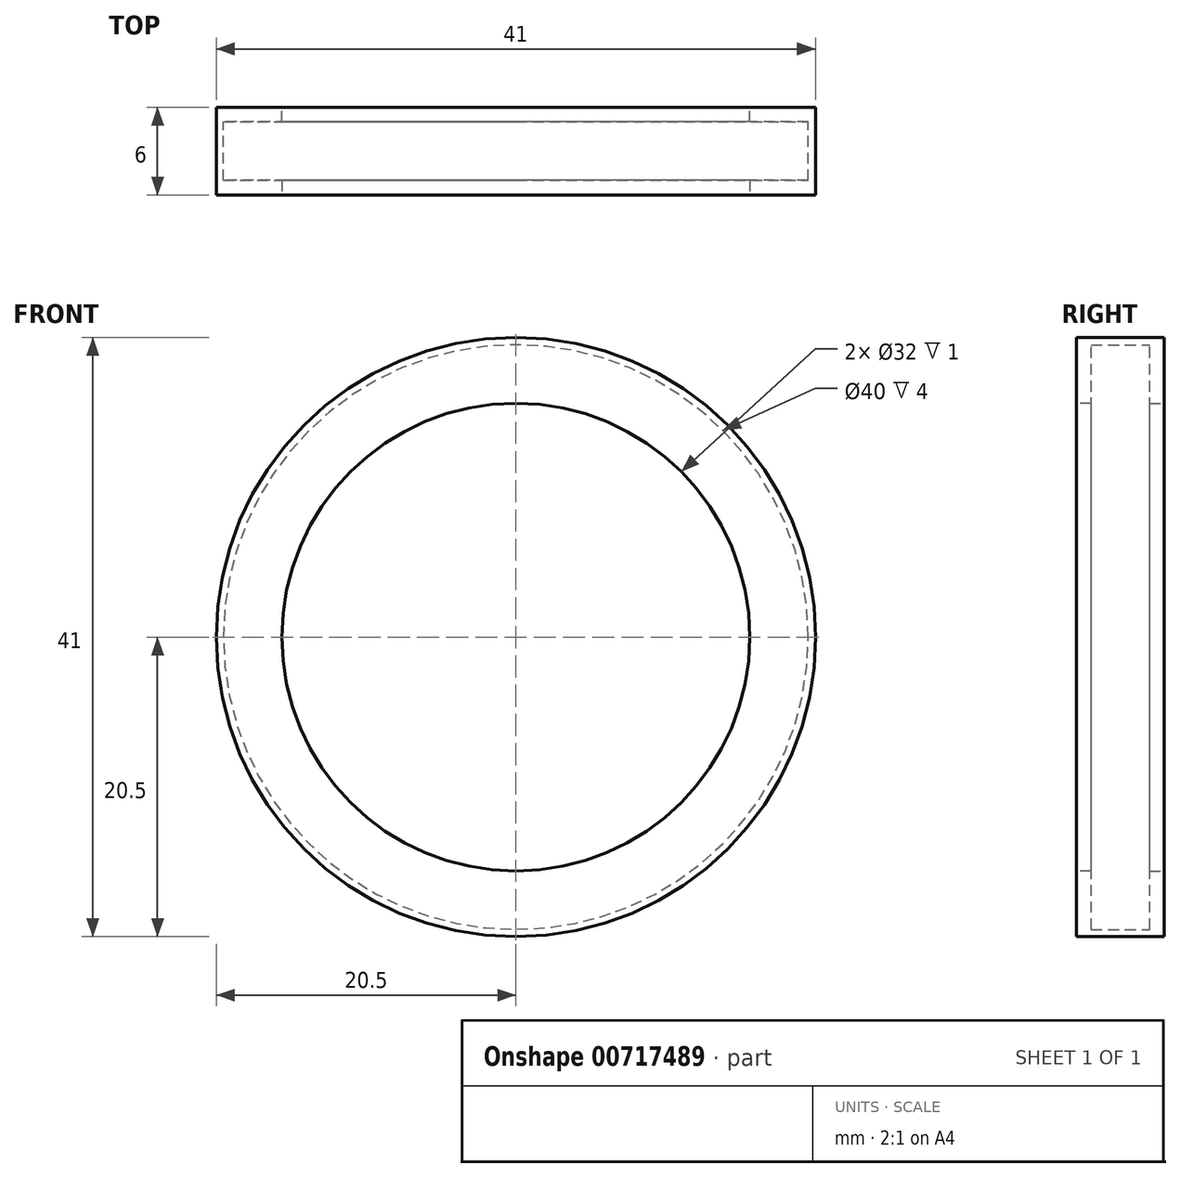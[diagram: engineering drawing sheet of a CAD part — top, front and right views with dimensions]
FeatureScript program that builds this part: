
annotation { "Feature Type Name" : "Feature", "Feature Type Description" : "" }
export const myFeature = defineFeature(function(context is Context, id is Id, definition is map)
    precondition{}
    {
        {
            var Q0;
            Q0=qCreatedBy(makeId("Front.planeOp"),FACE);
            var sketch = newSketch(context, id + "F0", { "sketchPlane" : qUnion([Q0])});
            skCircle(sketch, "E0", {"center": v(0, 0) * mm, "radius": 16 * mm});
            skCircle(sketch, "E1", {"center": v(0, 0) * mm, "radius": 20.5 * mm});
            skCircle(sketch, "E2", {"center": v(0, 0) * mm, "radius": 20 * mm});
            skSolve(sketch);
        }
        {
            var Q0;
            Q0=makeQuery(id+"F0.imprint","IMPRINT",FACE,{"disambiguationData":[TD([[makeQuery(id+"F0.imprint","IMPRINT",EDGE,{"derivedFrom":sQuery(id+"F0.wireOp",EDGE,"E1")}),1.0]])]});
            extrude(context, id + "F1", {"entities" : qUnion([Q0]), "depth" : 6 * mm, "offsetDistance" : 25 * mm});
        }
        {
            var Q0;
            Q0=makeQuery(id+"F0.imprint","IMPRINT",FACE,{"disambiguationData":[TD([[makeQuery(id+"F0.imprint","IMPRINT",EDGE,{"derivedFrom":sQuery(id+"F0.wireOp",EDGE,"E0")}),-1.0]])]});
            extrude(context, id + "F2", {"entities" : qUnion([Q0]), "operationType" : NewBodyOperationType.ADD, "depth" : 1 * mm, "offsetDistance" : 25 * mm});
        }
        {
            var Q0;
            Q0=makeQuery(id+"F1.opExtrude","CAP_FACE",FACE,{"disambiguationData":[OSD([sQuery(id+"F0.wireOp",EDGE,"E1"),sQuery(id+"F0.wireOp",EDGE,"E2")])],"isStart":false});
            var sketch = newSketch(context, id + "F3", { "sketchPlane" : qUnion([Q0])});
            skCircle(sketch, "E3", {"center": v(0, 0) * mm, "radius": 16 * mm});
            skSolve(sketch);
        }
        {
            var Q0;
            Q0=makeQuery(id+"F3.imprint","IMPRINT",FACE,{"disambiguationData":[TD([[makeQuery(id+"F3.imprint","IMPRINT",EDGE,{"derivedFrom":sQuery(id+"F3.wireOp",EDGE,"E3")}),-1.0]])]});
            extrude(context, id + "F4", {"entities" : qUnion([Q0]), "operationType" : NewBodyOperationType.ADD, "oppositeDirection" : true, "depth" : 1 * mm, "offsetDistance" : 25 * mm});
        }
    });
